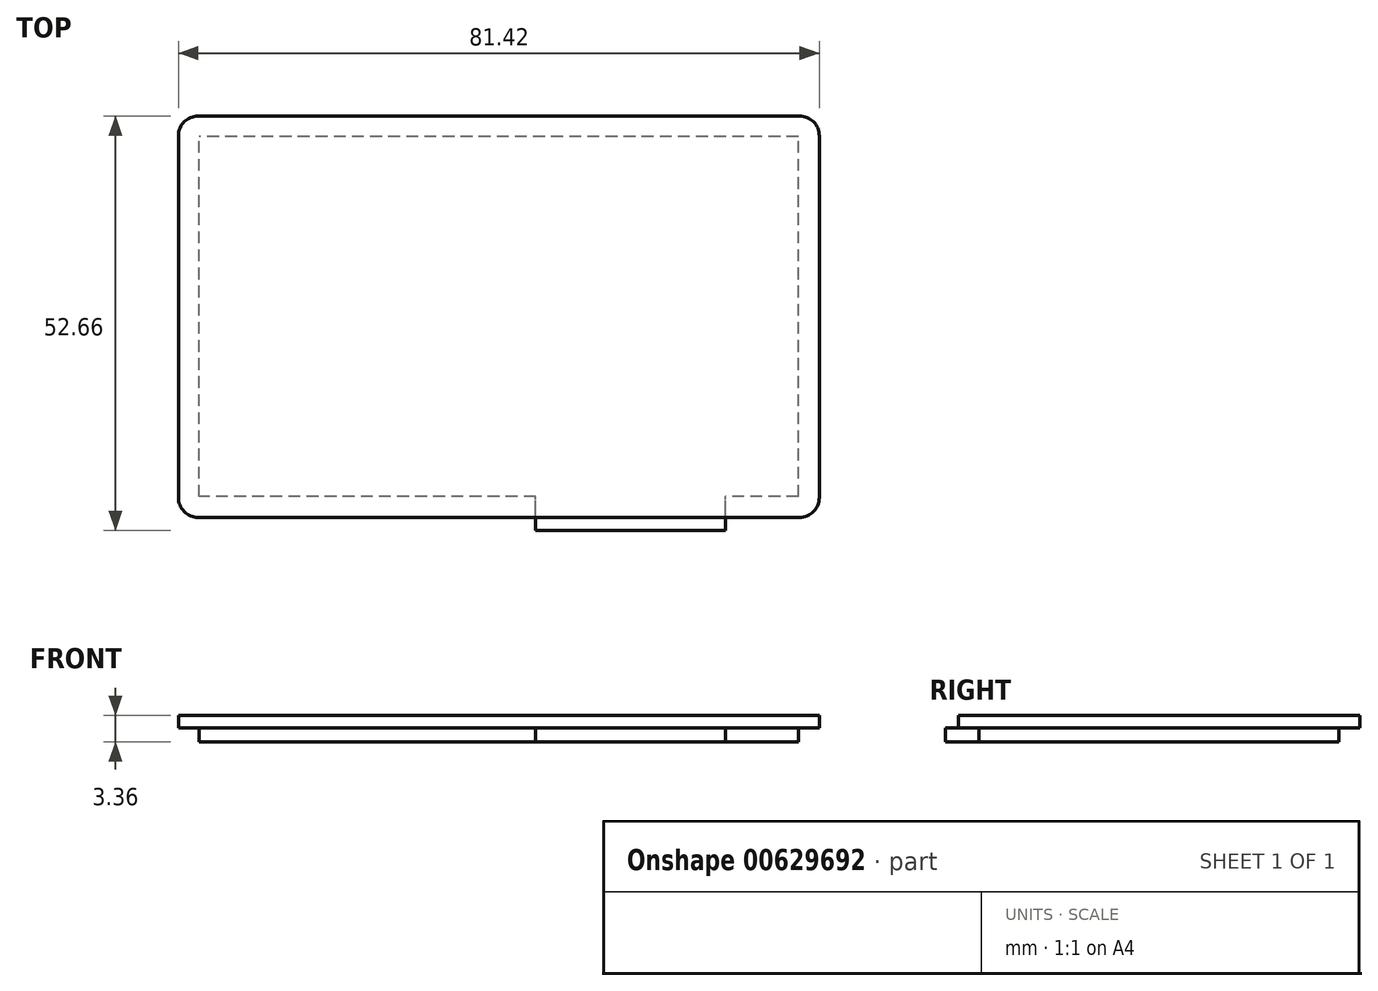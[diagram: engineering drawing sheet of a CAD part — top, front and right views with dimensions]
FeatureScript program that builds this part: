
annotation { "Feature Type Name" : "Feature", "Feature Type Description" : "" }
export const myFeature = defineFeature(function(context is Context, id is Id, definition is map)
    precondition{}
    {
        {
            var Q0;
            Q0=qCreatedBy(makeId("Top.planeOp"),FACE);
            var sketch = newSketch(context, id + "F0", { "sketchPlane" : qUnion([Q0])});
            skLineSegment(sketch, "E0.bottom", {"start": v(40.7, 25.5) * mm, "end": v(-40.7, 25.5) * mm});
            skLineSegment(sketch, "E0.top", {"start": v(40.7, -25.5) * mm, "end": v(-40.7, -25.5) * mm});
            skLineSegment(sketch, "E0.left", {"start": v(40.7, 25.5) * mm, "end": v(40.7, -25.5) * mm});
            skLineSegment(sketch, "E0.right", {"start": v(-40.7, 25.5) * mm, "end": v(-40.7, -25.5) * mm});
            skPoint(sketch, "E0.middle", {"position": v(0, 0) * mm});
            skSolve(sketch);
        }
        {
            var Q0;
            Q0 = qSketchRegion(id + "F0", true);
            extrude(context, id + "F1", {"entities" : qUnion([Q0]), "endBound" : BoundingType.SYMMETRIC, "depth" : 1.59 * mm, "offsetDistance" : 25.4 * mm});
        }
        {
            var Q0;
            Q0=makeQuery(id+"F1.opExtrude","SWEPT_EDGE",EDGE,{"disambiguationData":[OSD([sQuery(id+"F0.wireOp",EDGE,"E0.top"),sQuery(id+"F0.wireOp",EDGE,"E0.left")])]});
            var Q1;
            Q1=makeQuery(id+"F1.opExtrude","SWEPT_EDGE",EDGE,{"disambiguationData":[OSD([sQuery(id+"F0.wireOp",EDGE,"E0.bottom"),sQuery(id+"F0.wireOp",EDGE,"E0.left")])]});
            var Q2;
            Q2=makeQuery(id+"F1.opExtrude","SWEPT_EDGE",EDGE,{"disambiguationData":[OSD([sQuery(id+"F0.wireOp",EDGE,"E0.top"),sQuery(id+"F0.wireOp",EDGE,"E0.right")])]});
            var Q3;
            Q3=makeQuery(id+"F1.opExtrude","SWEPT_EDGE",EDGE,{"disambiguationData":[OSD([sQuery(id+"F0.wireOp",EDGE,"E0.bottom"),sQuery(id+"F0.wireOp",EDGE,"E0.right")])]});
            fillet(context, id + "F2", {"entities" : qUnion([Q0, Q1, Q2, Q3]), "radius" : 2.54 * mm, "tangentPropagation" : true, "allowEdgeOverflow" : false});
        }
        {
            var Q0;
            Q0=makeQuery(id+"F1.opExtrude","CAP_FACE",FACE,{"disambiguationData":[OSD([sQuery(id+"F0.wireOp",EDGE,"E0.bottom"),sQuery(id+"F0.wireOp",EDGE,"E0.top"),sQuery(id+"F0.wireOp",EDGE,"E0.left"),sQuery(id+"F0.wireOp",EDGE,"E0.right")])],"isStart":true});
            var sketch = newSketch(context, id + "F3", { "sketchPlane" : qUnion([Q0])});
            skLineSegment(sketch, "E1.bottom", {"start": v(38.05, 22.86) * mm, "end": v(-38.05, 22.86) * mm});
            skLineSegment(sketch, "E1.top", {"start": v(38.05, -22.86) * mm, "end": v(-38.05, -22.86) * mm});
            skLineSegment(sketch, "E1.left", {"start": v(38.05, 22.86) * mm, "end": v(38.05, -22.86) * mm});
            skLineSegment(sketch, "E1.right", {"start": v(-38.05, 22.86) * mm, "end": v(-38.05, -22.86) * mm});
            skPoint(sketch, "E1.middle", {"position": v(0, 0) * mm});
            skSolve(sketch);
        }
        {
            var Q0;
            Q0 = qSketchRegion(id + "F3", true);
            extrude(context, id + "F4", {"entities" : qUnion([Q0]), "operationType" : NewBodyOperationType.ADD, "depth" : 1.78 * mm, "offsetDistance" : 25.4 * mm});
        }
        {
            var Q0;
            Q0=makeQuery(id+"F1.opExtrude","CAP_FACE",FACE,{"disambiguationData":[OSD([sQuery(id+"F0.wireOp",EDGE,"E0.bottom"),sQuery(id+"F0.wireOp",EDGE,"E0.top"),sQuery(id+"F0.wireOp",EDGE,"E0.left"),sQuery(id+"F0.wireOp",EDGE,"E0.right")])],"isStart":true});
            var sketch = newSketch(context, id + "F5", { "sketchPlane" : qUnion([Q0])});
            skLineSegment(sketch, "E2.bottom", {"start": v(4.67, 16.64) * mm, "end": v(28.81, 16.64) * mm});
            skLineSegment(sketch, "E2.top", {"start": v(4.67, 27.16) * mm, "end": v(28.81, 27.16) * mm});
            skLineSegment(sketch, "E2.left", {"start": v(28.81, 27.16) * mm, "end": v(28.81, 16.64) * mm});
            skLineSegment(sketch, "E2.right", {"start": v(4.67, 27.16) * mm, "end": v(4.67, 16.64) * mm});
            skSolve(sketch);
        }
        {
            var Q0;
            Q0 = qSketchRegion(id + "F5", true);
            var Q1;
            Q1=makeQuery(id+"F4.opExtrude","CAP_FACE",FACE,{"disambiguationData":[OSD([sQuery(id+"F3.wireOp",EDGE,"E1.bottom"),sQuery(id+"F3.wireOp",EDGE,"E1.top"),sQuery(id+"F3.wireOp",EDGE,"E1.left"),sQuery(id+"F3.wireOp",EDGE,"E1.right")])],"isStart":false});
            extrude(context, id + "F6", {"entities" : qUnion([Q0]), "operationType" : NewBodyOperationType.ADD, "endBound" : BoundingType.UP_TO_SURFACE, "depth" : 25.4 * mm, "endBoundEntityFace" : qUnion([Q1]), "offsetDistance" : 25.4 * mm});
        }
    });
